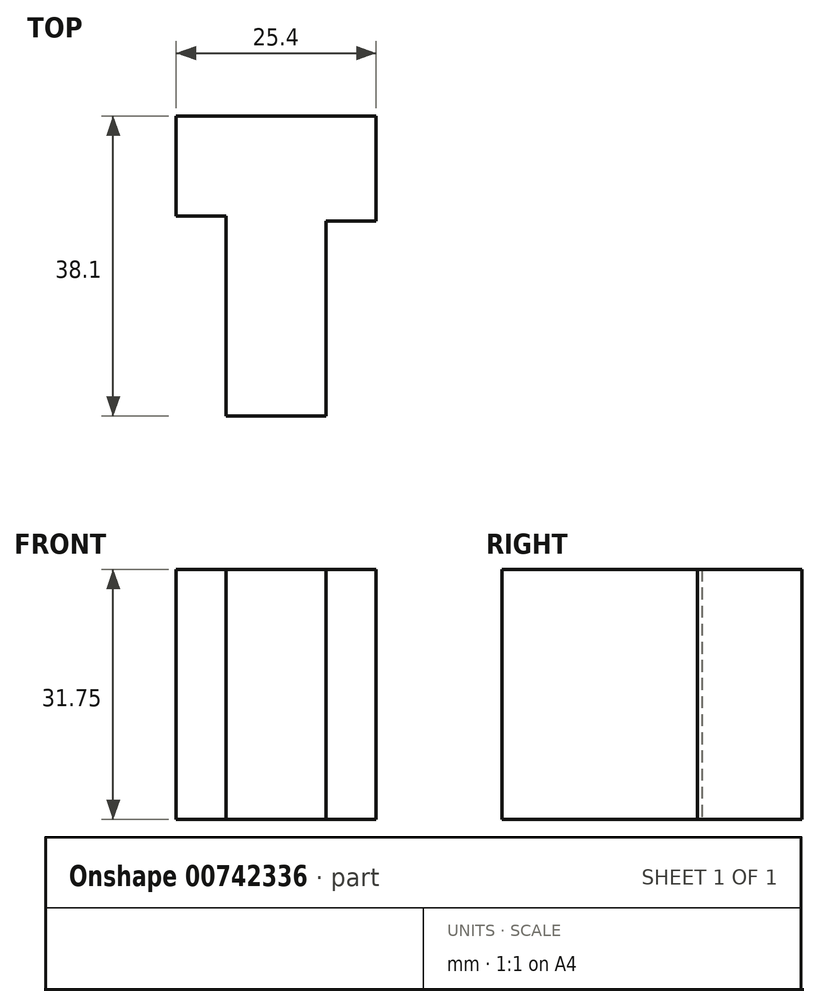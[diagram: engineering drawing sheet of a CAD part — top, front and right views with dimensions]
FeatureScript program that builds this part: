
annotation { "Feature Type Name" : "Feature", "Feature Type Description" : "" }
export const myFeature = defineFeature(function(context is Context, id is Id, definition is map)
    precondition{}
    {
        {
            var Q0;
            Q0=qCreatedBy(makeId("Top.planeOp"),FACE);
            var sketch = newSketch(context, id + "F0", { "sketchPlane" : qUnion([Q0])});
            skLineSegment(sketch, "E0", {"start": v(-6.35, 0) * mm, "end": v(-6.35, 24.8) * mm});
            skLineSegment(sketch, "E1", {"start": v(-6.35, 24.8) * mm, "end": v(0, 24.8) * mm});
            skLineSegment(sketch, "E2", {"start": v(0, 24.8) * mm, "end": v(0, 38.1) * mm});
            skLineSegment(sketch, "E3", {"start": v(0, 38.1) * mm, "end": v(-25.4, 38.1) * mm});
            skLineSegment(sketch, "E4", {"start": v(-25.4, 38.1) * mm, "end": v(-25.4, 25.4) * mm});
            skLineSegment(sketch, "E5", {"start": v(-25.4, 25.4) * mm, "end": v(-19.05, 25.4) * mm});
            skLineSegment(sketch, "E6", {"start": v(-19.05, 25.4) * mm, "end": v(-19.05, 0) * mm});
            skLineSegment(sketch, "E7", {"start": v(-19.05, 0) * mm, "end": v(-6.35, 0) * mm});
            skSolve(sketch);
        }
        {
            var Q0;
            Q0 = qSketchRegion(id + "F0", true);
            extrude(context, id + "F1", {"entities" : qUnion([Q0]), "depth" : 31.75 * mm, "offsetDistance" : 25.4 * mm});
        }
    });
